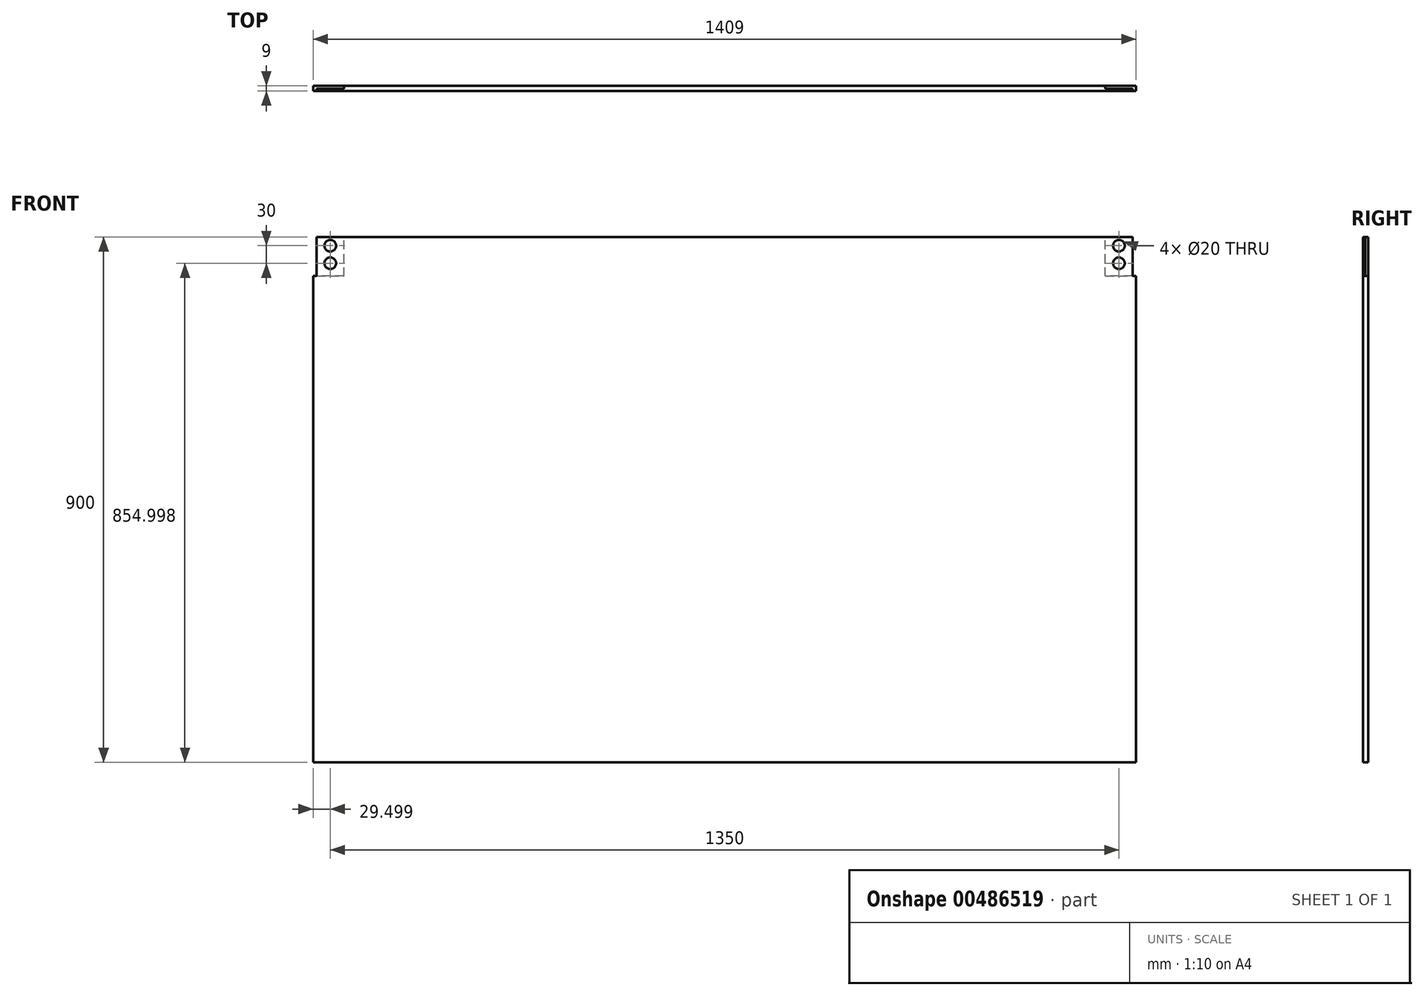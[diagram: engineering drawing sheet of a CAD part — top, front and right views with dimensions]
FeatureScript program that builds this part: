
annotation { "Feature Type Name" : "Feature", "Feature Type Description" : "" }
export const myFeature = defineFeature(function(context is Context, id is Id, definition is map)
    precondition{}
    {
        {
            var Q0;
            Q0=qCreatedBy(makeId("Front.planeOp"),FACE);
            var sketch = newSketch(context, id + "F0", { "sketchPlane" : qUnion([Q0])});
            skLineSegment(sketch, "E0.bottom", {"start": v(-682.57, 488.98) * mm, "end": v(714.43, 488.98) * mm});
            skLineSegment(sketch, "E0.top", {"start": v(-688.57, -411.02) * mm, "end": v(720.43, -411.02) * mm});
            skLineSegment(sketch, "E0.left", {"start": v(-688.57, 421.98) * mm, "end": v(-688.57, -411.02) * mm});
            skLineSegment(sketch, "E0.right", {"start": v(720.43, 421.98) * mm, "end": v(720.43, -411.02) * mm});
            skLineSegment(sketch, "E1", {"start": v(-682.57, 488.98) * mm, "end": v(-682.57, 421.98) * mm});
            skLineSegment(sketch, "E2", {"start": v(-682.57, 421.98) * mm, "end": v(-635.57, 421.98) * mm});
            skLineSegment(sketch, "E3", {"start": v(-635.57, 421.98) * mm, "end": v(-635.57, 488.98) * mm});
            skLineSegment(sketch, "E4", {"start": v(714.43, 488.98) * mm, "end": v(714.43, 421.98) * mm});
            skLineSegment(sketch, "E5", {"start": v(714.43, 421.98) * mm, "end": v(667.43, 421.98) * mm});
            skLineSegment(sketch, "E6", {"start": v(667.43, 421.98) * mm, "end": v(667.43, 488.98) * mm});
            skLineSegment(sketch, "E7", {"start": v(714.43, 421.98) * mm, "end": v(720.43, 421.98) * mm});
            skCircle(sketch, "E8", {"center": v(-659.07, 473.98) * mm, "radius": 10 * mm});
            skCircle(sketch, "E9", {"center": v(-659.07, 443.98) * mm, "radius": 10 * mm});
            skCircle(sketch, "E10", {"center": v(690.93, 473.98) * mm, "radius": 10 * mm});
            skCircle(sketch, "E11", {"center": v(690.93, 443.98) * mm, "radius": 10 * mm});
            skLineSegment(sketch, "E12", {"start": v(-682.57, 421.98) * mm, "end": v(-688.57, 421.98) * mm});
            skSolve(sketch);
        }
        {
            var Q0;
            {var subQ1=sQuery(id+"F0.wireOp",EDGE,"E0.top");Q0=makeQuery(id+"F0.imprint","IMPRINT",FACE,{"disambiguationData":[TD([[makeQuery(id+"F0.imprint","IMPRINT",EDGE,{"derivedFrom":subQ1}),1.0]])]});}
            var Q1;
            {var subQ0=sQuery(id+"F0.wireOp",EDGE,"E1");Q1=makeQuery(id+"F0.imprint","IMPRINT",FACE,{"disambiguationData":[TD([[makeQuery(id+"F0.imprint","IMPRINT",EDGE,{"derivedFrom":subQ0}),1.0]])]});}
            var Q2;
            {var subQ0=sQuery(id+"F0.wireOp",EDGE,"E4");Q2=makeQuery(id+"F0.imprint","IMPRINT",FACE,{"disambiguationData":[TD([[makeQuery(id+"F0.imprint","IMPRINT",EDGE,{"derivedFrom":subQ0}),-1.0]])]});}
            extrude(context, id + "F1", {"entities" : qUnion([Q0, Q1, Q2]), "depth" : 9 * mm, "offsetDistance" : 25 * mm});
        }
        {
            var Q0;
            {var subQ0=sQuery(id+"F0.wireOp",EDGE,"E1");Q0=makeQuery(id+"F0.imprint","IMPRINT",FACE,{"disambiguationData":[TD([[makeQuery(id+"F0.imprint","IMPRINT",EDGE,{"derivedFrom":subQ0}),1.0]])]});}
            var Q1;
            {var subQ0=sQuery(id+"F0.wireOp",EDGE,"E4");Q1=makeQuery(id+"F0.imprint","IMPRINT",FACE,{"disambiguationData":[TD([[makeQuery(id+"F0.imprint","IMPRINT",EDGE,{"derivedFrom":subQ0}),-1.0]])]});}
            extrude(context, id + "F2", {"entities" : qUnion([Q0, Q1]), "operationType" : NewBodyOperationType.REMOVE, "depth" : 5 * mm, "offsetDistance" : 25 * mm});
        }
    });
